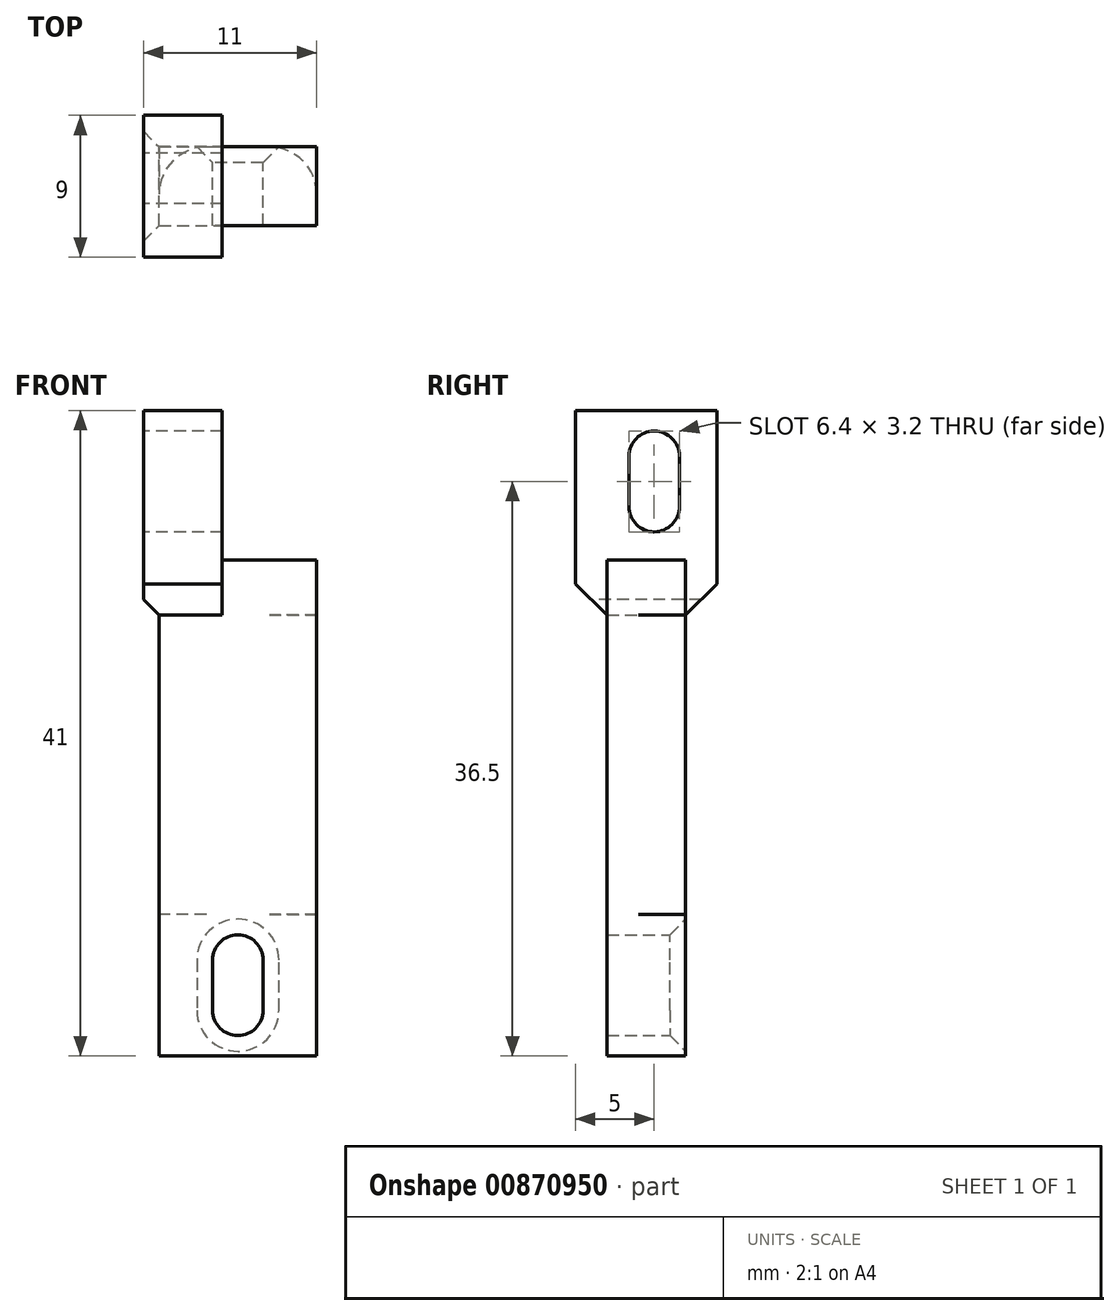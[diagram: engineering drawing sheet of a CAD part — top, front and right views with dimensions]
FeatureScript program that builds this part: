
annotation { "Feature Type Name" : "Feature", "Feature Type Description" : "" }
export const myFeature = defineFeature(function(context is Context, id is Id, definition is map)
    precondition{}
    {
        {
            var Q0;
            Q0=qCreatedBy(makeId("Front.planeOp"),FACE);
            var sketch = newSketch(context, id + "F0", { "sketchPlane" : qUnion([Q0])});
            skLineSegment(sketch, "E0.bottom", {"start": v(0, 0) * mm, "end": v(10, 0) * mm});
            skLineSegment(sketch, "E0.top", {"start": v(4, 31.5) * mm, "end": v(10, 31.5) * mm});
            skLineSegment(sketch, "E0.left", {"start": v(0, 0) * mm, "end": v(0, 28) * mm});
            skLineSegment(sketch, "E0.right", {"start": v(10, 0) * mm, "end": v(10, 31.5) * mm});
            skLineSegment(sketch, "E1", {"start": v(10, 15.75) * mm, "end": v(0, 15.75) * mm, "construction": true});
            skLineSegment(sketch, "E2", {"start": v(5, 15.75) * mm, "end": v(5, 27) * mm, "construction": true});
            skLineSegment(sketch, "E3", {"start": v(5, 15.75) * mm, "end": v(5, 4.5) * mm, "construction": true});
            skArc(sketch, "E4", {"start": v(6.6, 6.1) * mm, "mid": v(5, 7.7) * mm, "end": v(3.4, 6.1) * mm});
            skArc(sketch, "E5", {"start": v(3.4, 2.9) * mm, "mid": v(5, 1.3) * mm, "end": v(6.6, 2.9) * mm});
            skPoint(sketch, "E5.centerSnap0", {"position": v(5, 0) * mm});
            skLineSegment(sketch, "E6", {"start": v(3.4, 6.1) * mm, "end": v(3.4, 2.9) * mm});
            skLineSegment(sketch, "E7", {"start": v(6.6, 6.1) * mm, "end": v(6.6, 2.9) * mm});
            skLineSegment(sketch, "E8", {"start": v(4, 31.5) * mm, "end": v(4, 41) * mm});
            skLineSegment(sketch, "E9", {"start": v(4, 41) * mm, "end": v(-1, 41) * mm});
            skLineSegment(sketch, "E10", {"start": v(-1, 41) * mm, "end": v(-1, 28) * mm});
            skLineSegment(sketch, "E11", {"start": v(-1, 28) * mm, "end": v(0, 28) * mm});
            skPoint(sketch, "E12.orphan", {"position": v(0, 31.5) * mm});
            skSolve(sketch);
        }
        {
            var Q0;
            Q0=makeQuery(id+"F0.imprint","IMPRINT",FACE,{"disambiguationData":[TD([[makeQuery(id+"F0.imprint","IMPRINT",EDGE,{"derivedFrom":sQuery(id+"F0.wireOp",EDGE,"E0.bottom")}),1.0]])]});
            extrude(context, id + "F1", {"entities" : qUnion([Q0]), "depth" : 5 * mm, "offsetDistance" : 25 * mm});
        }
        {
            var Q0;
            Q0=qCreatedBy(makeId("Top.planeOp"),FACE);
            cPlane(context, id + "F2", {"entities" : qUnion([Q0]), "cplaneType" : CPlaneType.OFFSET, "offset" : 9 * mm, "width" : 150 * mm, "height" : 150 * mm});
        }
        {
            var Q0;
            Q0=makeQuery(id+"F1.opExtrude","CAP_FACE",FACE,{"disambiguationData":[OSD([sQuery(id+"F0.wireOp",EDGE,"E0.bottom"),sQuery(id+"F0.wireOp",EDGE,"E0.top"),sQuery(id+"F0.wireOp",EDGE,"E0.left"),sQuery(id+"F0.wireOp",EDGE,"E0.right"),sQuery(id+"F0.wireOp",EDGE,"E4"),sQuery(id+"F0.wireOp",EDGE,"E5"),sQuery(id+"F0.wireOp",EDGE,"E6"),sQuery(id+"F0.wireOp",EDGE,"E7"),sQuery(id+"F0.wireOp",EDGE,"E8"),sQuery(id+"F0.wireOp",EDGE,"E9"),sQuery(id+"F0.wireOp",EDGE,"E10"),sQuery(id+"F0.wireOp",EDGE,"E11")])],"isStart":true});
            var sketch = newSketch(context, id + "F3", { "sketchPlane" : qUnion([Q0])});
            skLineSegment(sketch, "E13.bottom", {"start": v(1, 41) * mm, "end": v(-4, 41) * mm});
            skLineSegment(sketch, "E13.top", {"start": v(1, 28) * mm, "end": v(-4, 28) * mm});
            skLineSegment(sketch, "E13.left", {"start": v(1, 41) * mm, "end": v(1, 28) * mm});
            skLineSegment(sketch, "E13.right", {"start": v(-4, 41) * mm, "end": v(-4, 28) * mm});
            skSolve(sketch);
        }
        {
            var Q0;
            {var subQ5=sQuery(id+"F3.wireOp",EDGE,"E13.bottom");Q0=makeQuery(id+"F3.imprint","IMPRINT",FACE,{"disambiguationData":[TD([[makeQuery(id+"F3.imprint","IMPRINT",EDGE,{"derivedFrom":subQ5}),-1.0]])]});}
            extrude(context, id + "F4", {"entities" : qUnion([Q0]), "operationType" : NewBodyOperationType.ADD, "depth" : 2 * mm, "offsetDistance" : 25 * mm, "hasSecondDirection" : true, "secondDirectionOppositeDirection" : true, "secondDirectionDepth" : 7 * mm});
        }
        {
            var Q0;
            Q0=makeQuery(id+"F4.boolean.opBoolean","MERGE",FACE,{"derivedFrom":[makeQuery(id+"F1.opExtrude","SWEPT_FACE",FACE,{"disambiguationData":[OSD([sQuery(id+"F0.wireOp",EDGE,"E10")])]}),makeQuery(id+"F4.opExtrude","SWEPT_FACE",FACE,{"disambiguationData":[OSD([sQuery(id+"F3.wireOp",EDGE,"E13.left")])]})]});
            var sketch = newSketch(context, id + "F5", { "sketchPlane" : qUnion([Q0])});
            skArc(sketch, "E14", {"start": v(3.6, 38.1) * mm, "mid": v(2, 39.7) * mm, "end": v(0.4, 38.1) * mm});
            skPoint(sketch, "E14.centerSnap0", {"position": v(2.5, 41) * mm});
            skArc(sketch, "E15", {"start": v(0.4, 34.9) * mm, "mid": v(2, 33.3) * mm, "end": v(3.6, 34.9) * mm});
            skLineSegment(sketch, "E16", {"start": v(0.4, 38.1) * mm, "end": v(0.4, 34.9) * mm});
            skLineSegment(sketch, "E17", {"start": v(3.6, 38.1) * mm, "end": v(3.6, 34.9) * mm});
            skSolve(sketch);
        }
        {
            var Q0;
            Q0=makeQuery(id+"F5.imprint","IMPRINT",FACE,{"disambiguationData":[TD([[makeQuery(id+"F5.imprint","IMPRINT",EDGE,{"derivedFrom":sQuery(id+"F5.wireOp",EDGE,"E14")}),1.0]])]});
            extrude(context, id + "F6", {"entities" : qUnion([Q0]), "operationType" : NewBodyOperationType.REMOVE, "oppositeDirection" : true, "depth" : 25 * mm, "offsetDistance" : 25 * mm});
        }
        {
            var Q0;
            Q0=makeQuery(id+"F4.opExtrude","CAP_EDGE",EDGE,{"disambiguationData":[OSD([sQuery(id+"F3.wireOp",EDGE,"E13.top")])],"isStart":false});
            var Q1;
            Q1=makeQuery(id+"F4.opExtrude","CAP_EDGE",EDGE,{"disambiguationData":[OSD([sQuery(id+"F3.wireOp",EDGE,"E13.top")])],"isStart":true});
            chamfer(context, id + "F7", {"entities" : qUnion([Q0, Q1]), "width" : 2 * mm, "tangentPropagation" : true});
        }
        {
            var Q0;
            Q0=makeQuery(id+"F4.boolean.opBoolean","MERGE",EDGE,{"derivedFrom":[makeQuery(id+"F1.opExtrude","SWEPT_EDGE",EDGE,{"disambiguationData":[OSD([sQuery(id+"F0.wireOp",EDGE,"E10"),sQuery(id+"F0.wireOp",EDGE,"E11")])]}),makeQuery(id+"F4.opExtrude","SWEPT_EDGE",EDGE,{"disambiguationData":[OSD([sQuery(id+"F3.wireOp",EDGE,"E13.top"),sQuery(id+"F3.wireOp",EDGE,"E13.left")])]})]});
            chamfer(context, id + "F8", {"entities" : qUnion([Q0]), "width" : 1 * mm, "tangentPropagation" : true});
        }
        {
            var Q0;
            Q0=qCreatedBy(id+"F2.planeOp",FACE);
            var sketch = newSketch(context, id + "F9", { "sketchPlane" : qUnion([Q0])});
            skPoint(sketch, "E18.0", {"position": v(0, -2.5) * mm});
            skLineSegment(sketch, "E19.0", {"start": v(10, -5) * mm, "end": v(10, -3) * mm});
            skLineSegment(sketch, "E20.0", {"start": v(0, -5) * mm, "end": v(0, -3) * mm});
            skLineSegment(sketch, "E21.0", {"start": v(3, 0) * mm, "end": v(7, 0) * mm});
            skPoint(sketch, "E22.visualSharp", {"position": v(10, 0) * mm});
            skArc(sketch, "E22.filletArc", {"start": v(10, -3) * mm, "mid": v(9.12, -0.88) * mm, "end": v(7, 0) * mm});
            skPoint(sketch, "E23.visualSharp", {"position": v(0, 0) * mm});
            skArc(sketch, "E23.filletArc", {"start": v(3, 0) * mm, "mid": v(0.88, -0.88) * mm, "end": v(0, -3) * mm});
            skLineSegment(sketch, "E24", {"start": v(10, -3) * mm, "end": v(10, 0) * mm});
            skLineSegment(sketch, "E25", {"start": v(7, 0) * mm, "end": v(10, 0) * mm});
            skLineSegment(sketch, "E26", {"start": v(3, 0) * mm, "end": v(0, 0) * mm});
            skLineSegment(sketch, "E27", {"start": v(0, 0) * mm, "end": v(0, -3) * mm});
            skSolve(sketch);
        }
        {
            var Q0;
            Q0 = qSketchRegion(id + "F9", true);
            extrude(context, id + "F10", {"entities" : qUnion([Q0]), "operationType" : NewBodyOperationType.REMOVE, "depth" : 19 * mm, "offsetDistance" : 25 * mm});
        }
        {
            var Q0;
            Q0=makeQuery(id+"F1.opExtrude","CAP_EDGE",EDGE,{"disambiguationData":[OSD([sQuery(id+"F0.wireOp",EDGE,"E7")])],"isStart":true});
            var Q1;
            Q1=makeQuery(id+"F6.boolean.opBoolean","COPY",EDGE,{"derivedFrom":makeQuery(id+"F6.opExtrude","CAP_EDGE",EDGE,{"disambiguationData":[OSD([sQuery(id+"F5.wireOp",EDGE,"E17")])],"isStart":true})});
            chamfer(context, id + "F11", {"entities" : qUnion([Q0, Q1]), "width" : 1 * mm, "tangentPropagation" : true});
        }
    });
